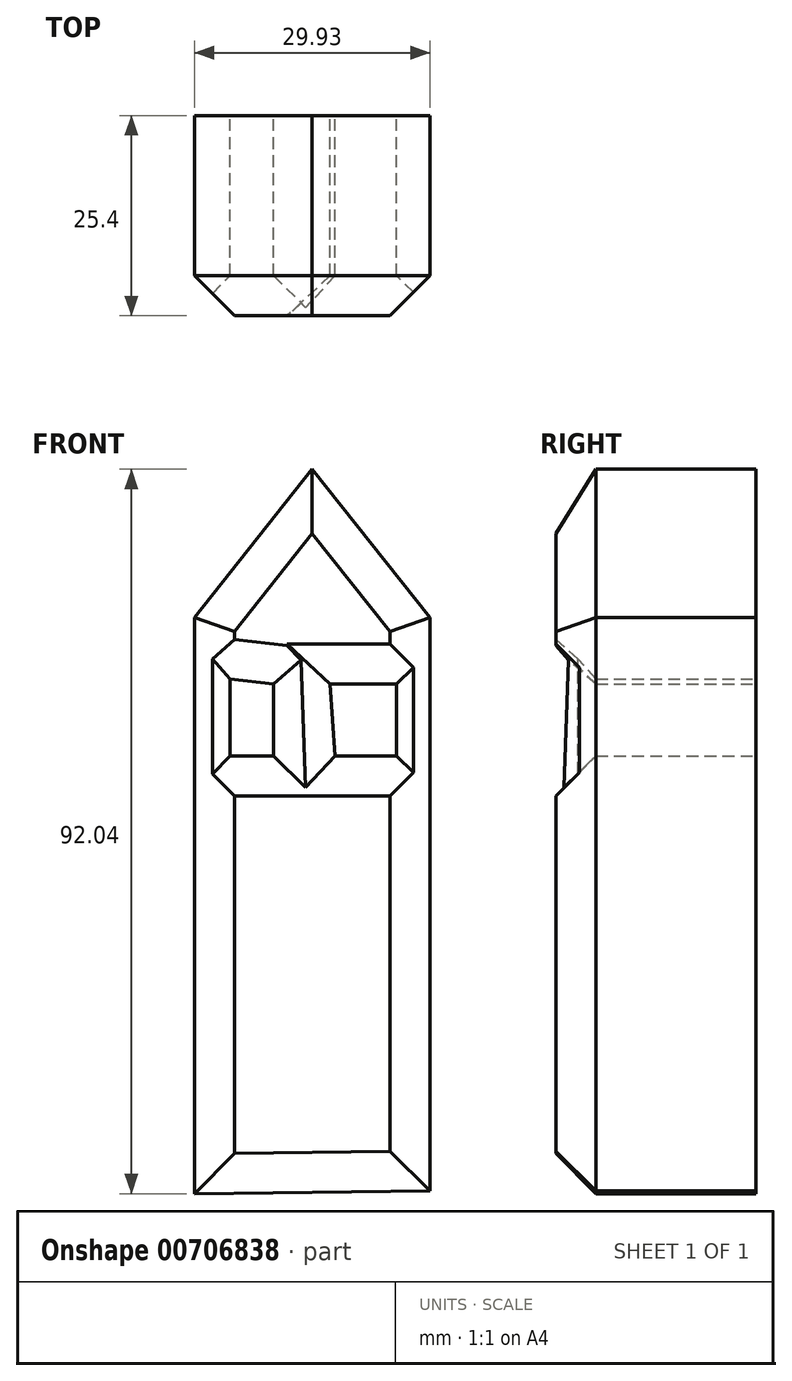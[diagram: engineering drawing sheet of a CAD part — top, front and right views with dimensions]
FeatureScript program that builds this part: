
annotation { "Feature Type Name" : "Feature", "Feature Type Description" : "" }
export const myFeature = defineFeature(function(context is Context, id is Id, definition is map)
    precondition{}
    {
        {
            var Q0;
            Q0=qCreatedBy(makeId("Front.planeOp"),FACE);
            var sketch = newSketch(context, id + "F0", { "sketchPlane" : qUnion([Q0])});
            skLineSegment(sketch, "E0", {"start": v(-38.87, -36.59) * mm, "end": v(-38.87, 36.59) * mm});
            skLineSegment(sketch, "E1", {"start": v(-38.87, 36.59) * mm, "end": v(-23.9, 55.45) * mm});
            skLineSegment(sketch, "E2", {"start": v(-23.9, 55.45) * mm, "end": v(-8.94, 36.59) * mm});
            skLineSegment(sketch, "E3", {"start": v(-8.94, 36.59) * mm, "end": v(-8.94, -36.26) * mm});
            skLineSegment(sketch, "E4", {"start": v(-38.87, -36.59) * mm, "end": v(-8.94, -36.26) * mm});
            skLineSegment(sketch, "E5", {"start": v(-38.87, 36.59) * mm, "end": v(-8.94, 36.59) * mm});
            skLineSegment(sketch, "E6", {"start": v(-34.31, 28.78) * mm, "end": v(-34.31, 19.03) * mm});
            skLineSegment(sketch, "E7", {"start": v(-34.31, 19.03) * mm, "end": v(-28.78, 19.03) * mm});
            skLineSegment(sketch, "E8", {"start": v(-28.78, 19.03) * mm, "end": v(-28.78, 28.13) * mm});
            skLineSegment(sketch, "E9", {"start": v(-28.78, 28.13) * mm, "end": v(-34.31, 28.78) * mm});
            skLineSegment(sketch, "E10", {"start": v(-21.63, 28.13) * mm, "end": v(-13.17, 28.13) * mm});
            skLineSegment(sketch, "E11", {"start": v(-13.17, 28.13) * mm, "end": v(-13.17, 19.03) * mm});
            skLineSegment(sketch, "E12", {"start": v(-13.17, 19.03) * mm, "end": v(-20.98, 19.03) * mm});
            skLineSegment(sketch, "E13", {"start": v(-20.98, 19.03) * mm, "end": v(-21.63, 28.13) * mm});
            skSolve(sketch);
        }
        {
            var Q0;
            Q0 = qSketchRegion(id + "F0", true);
            extrude(context, id + "F1", {"entities" : qUnion([Q0]), "depth" : 25.4 * mm, "offsetDistance" : 25.4 * mm});
        }
        {
            var Q0;
            Q0=makeQuery(id+"F1.opExtrude","CAP_FACE",FACE,{"disambiguationData":[OSD([sQuery(id+"F0.wireOp",EDGE,"E0"),sQuery(id+"F0.wireOp",EDGE,"E1"),sQuery(id+"F0.wireOp",EDGE,"E2"),sQuery(id+"F0.wireOp",EDGE,"E3"),sQuery(id+"F0.wireOp",EDGE,"E4"),sQuery(id+"F0.wireOp",EDGE,"E6"),sQuery(id+"F0.wireOp",EDGE,"E7"),sQuery(id+"F0.wireOp",EDGE,"E8"),sQuery(id+"F0.wireOp",EDGE,"E9"),sQuery(id+"F0.wireOp",EDGE,"E10"),sQuery(id+"F0.wireOp",EDGE,"E11"),sQuery(id+"F0.wireOp",EDGE,"E12"),sQuery(id+"F0.wireOp",EDGE,"E13")])],"isStart":false});
            chamfer(context, id + "F2", {"entities" : qUnion([Q0]), "width" : 5.08 * mm, "tangentPropagation" : true});
        }
        {
            var Q0;
            Q0=qCreatedBy(makeId("Front.planeOp"),FACE);
            var sketch = newSketch(context, id + "F3", { "sketchPlane" : qUnion([Q0])});
            skLineSegment(sketch, "E14", {"start": v(-28.46, -20.33) * mm, "end": v(-28.46, 0) * mm});
            skLineSegment(sketch, "E15", {"start": v(-28.46, 0) * mm, "end": v(-17.4, 0) * mm});
            skLineSegment(sketch, "E16", {"start": v(-17.4, 0) * mm, "end": v(-17.4, -19.68) * mm});
            skLineSegment(sketch, "E17", {"start": v(-17.4, -19.68) * mm, "end": v(-28.46, -20.33) * mm});
            skCircle(sketch, "E18", {"center": v(-20.4, -8.73) * mm, "radius": 2.43 * mm});
            skSolve(sketch);
        }
        {
            var Q0;
            Q0 = qSketchRegion(id + "F3", true);
            extrude(context, id + "F4", {"entities" : qUnion([Q0]), "operationType" : NewBodyOperationType.ADD, "depth" : 25.4 * mm, "offsetDistance" : 25.4 * mm});
        }
    });
